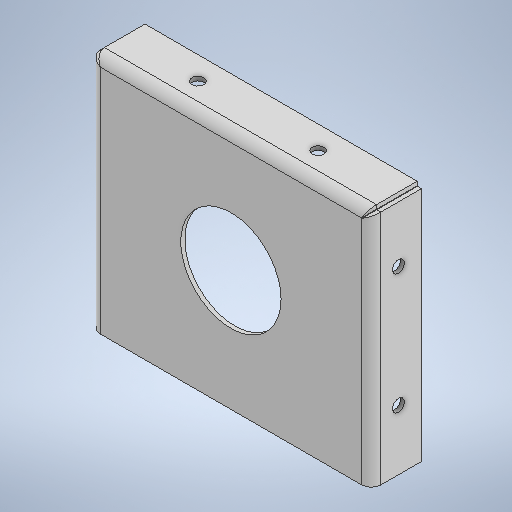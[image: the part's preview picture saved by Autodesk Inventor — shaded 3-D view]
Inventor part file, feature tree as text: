
AUTODESK INVENTOR PART (.ipt)
format: ipt  version: 2025 (Build 290162010, 162A)  size: 303,104 bytes
history: native  units: mm
features: sketch x4, extrude x3, sheet_metal_op x3, other x2
ambient origin geometry x8: Origin, YZ Plane, XZ Plane, XY Plane, X Axis, Y Axis, Z Axis, Center Point
bodies: Solid1 (feature_tree)
feature tree (12):
  extrude  "Extrusion1"  Depth=2.0mm TaperAngle=0.0deg
  other  "A-Side Definition"
  sheet_metal_op  "Flange1"
  extrude  "Extrusion2"  Depth=120.0mm
  extrude  "Extrusion3"  Depth=2.0mm
  sketch  "Sketch1"  dims[d4=140.0mm d5=2.0mm d6=0.0mm]
  sketch  "Sketch2"  dims[d13=50.0mm d14=120.0mm]
  other  "Plate1"
  sheet_metal_op  "Bend1"
  sheet_metal_op  "Corner1"
  sketch  "Sketch3"  dims[d15=60.0mm d16=2.0mm]
  sketch  "Sketch4"  dims[d17=2.0mm d18=1.0mm d19=4.0mm d20=2.75mm d21=25.0mm d22=90.0deg d23=2.75mm d24=8.0mm d25=0.2mm d26=2.75mm d27=6.0mm d28=60.0mm d29=0.0mm d30=0.0mm d31=6.0mm d32=60.0mm d34=0.0mm d35=0.0mm d33=0.5mm]
